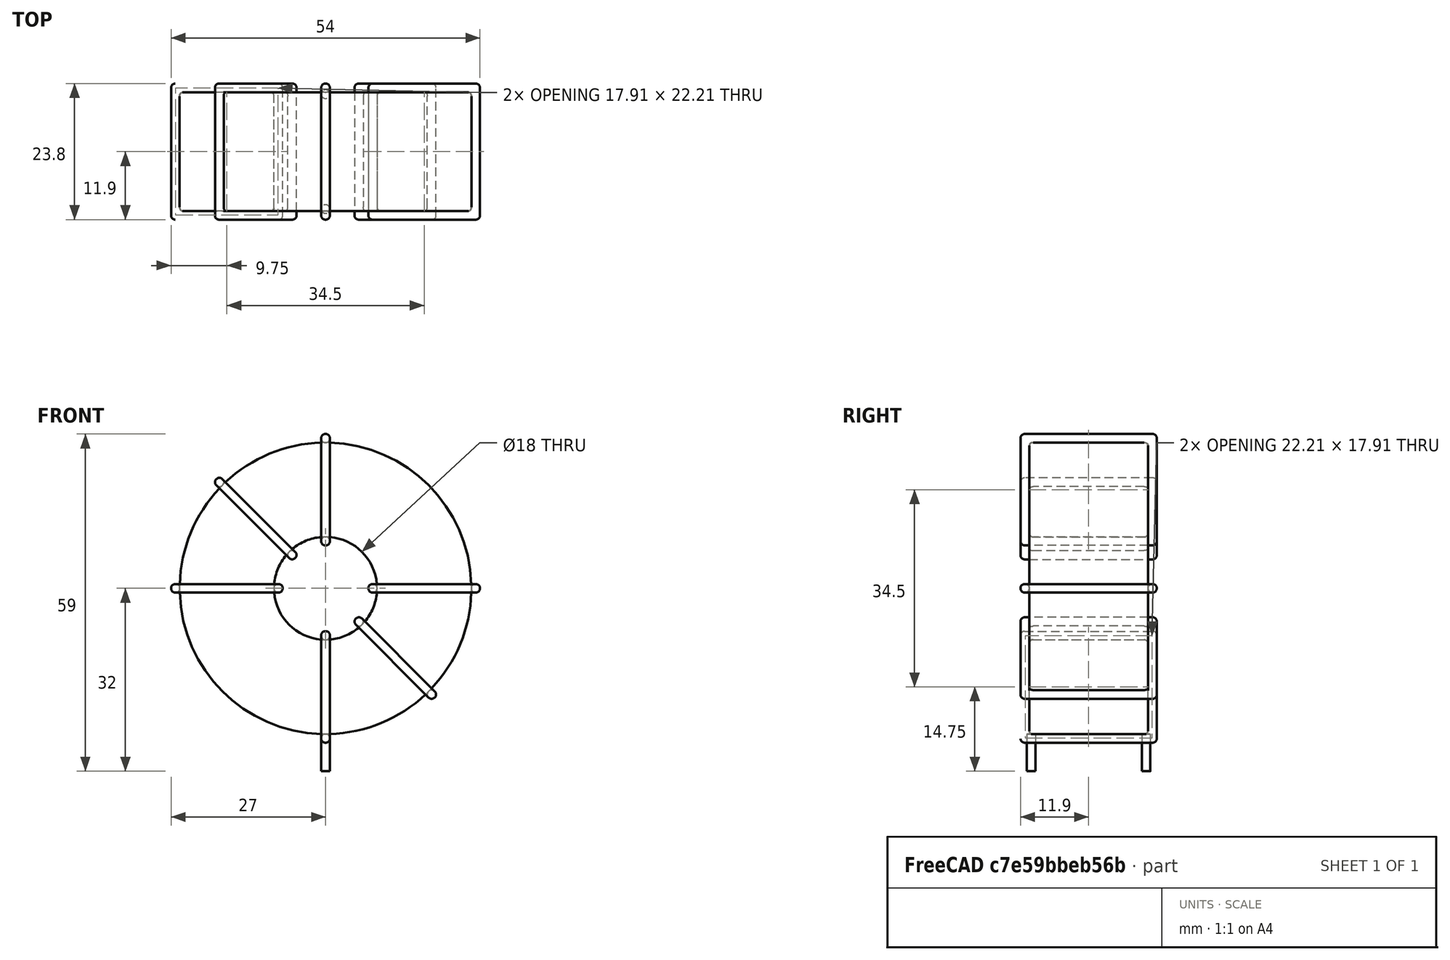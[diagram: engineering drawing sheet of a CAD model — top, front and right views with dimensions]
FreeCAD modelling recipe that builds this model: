
FCSTD DOCUMENT  (FreeCAD 0.16R6703 (Git))
Label: L_Toroid_Vertical_L54.0mm_W23.8mm_P20.10mm_Bourns_5700series
License: All rights reserved
LicenseURL: http://en.wikipedia.org/wiki/All_rights_reserved
objects: Sketcher::SketchObject×6, PartDesign::Pad×6, PartDesign::Fillet×5, Spreadsheet::Sheet×1
note: 23 computed .brp shape members not serialized (recipe doc carries the construction recipe); baked Part::Feature solids carry a one-line shape summary decoded from their .brp

FEATURE [Spreadsheet::Sheet] Spreadsheet  label="dimensions"
  cells = A1=Wx; B1(Wx)=54; C1(WW)=18; D1=54; A2=Wy; B2(Wy)=23.8; D2=23.8; A3=RM; B3(RMx)=20.1; C3(RMy)=0; A4=d_wire; B4(d_wire)=1.5; A5=H; B5(H)=54; A6=offsetx; B6(offsetx)=27
FEATURE [Sketcher::SketchObject] Sketch
  Placement = pos=(0,-10.05,0) rot=(1,0,0;1.5708rad)
  expr: Placement.Base.y = -Spreadsheet.RMx / 2
  expr: Constraints[0] = Spreadsheet.Wx / 2 - Spreadsheet.d_wire
  expr: Constraints[4] = Spreadsheet.WW / 2
  expr: Constraints[2] = Spreadsheet.Wx / 2 + Spreadsheet.d_wire + 0.5
  sketch-geometry (2):
    g0: Circle CenterX=0 CenterY=29 CenterZ=0 NormalX=0 NormalY=0 NormalZ=1 Radius=25.5
    g1: Circle CenterX=0 CenterY=29 CenterZ=0 NormalX=0 NormalY=0 NormalZ=1 Radius=9
  constraints (5):
    c: Radius(g0) = 25.5
    c: DistanceX(g-1,g0) = 0
    c: DistanceY(g-1,g0) = 29
    c: Coincident(g1,g0)
    c: Radius(g1) = 9
FEATURE [PartDesign::Pad] Pad
  Length = 20.8
  Length2 = 100
  Midplane = true
  Placement = pos=(0,-10.05,0) rot=(1,0,0;1.5708rad)
  Sketch = -> Sketch
  Type = 0
  expr: Length = Spreadsheet.Wy - 2 * Spreadsheet.d_wire
FEATURE [Sketcher::SketchObject] Sketch001
  Placement = pos=(0,0,2) rot=(0,0,1;0rad)
  expr: Placement.Base.z = 0.5 + Spreadsheet.d_wire
  expr: Constraints[4] = Spreadsheet.RMy
  expr: Constraints[2] = -Spreadsheet.RMx
  expr: Constraints[1] = Spreadsheet.d_wire / 2
  sketch-geometry (2):
    g0: Circle CenterX=0 CenterY=0 CenterZ=0 NormalX=0 NormalY=0 NormalZ=1 Radius=0.75
    g1: Circle CenterX=0 CenterY=-20.1 CenterZ=0 NormalX=0 NormalY=0 NormalZ=1 Radius=0.75
  constraints (5):
    c: Equal(g0,g1)
    c: Radius(g0) = 0.75
    c: DistanceY(g-1,g1) = -20.1
    c: Coincident(g0,g-1)
    c: DistanceX(g-1,g1) = 0
FEATURE [PartDesign::Pad] Pad001
  Length = 1.5
  Length2 = 5
  Placement = pos=(0,0,2) rot=(0,0,1;0rad)
  Reversed = true
  Sketch = -> Sketch001
  Type = 4
  expr: Length2 = 3.5 + Spreadsheet.d_wire
  expr: Length = Spreadsheet.d_wire
FEATURE [PartDesign::Fillet] Fillet
  Base = -> Pad [Edge6,Edge3,Edge2]
  Placement = pos=(0,-10.05,0) rot=(1,0,0;1.5708rad)
  Radius = 0.5
FEATURE [Sketcher::SketchObject] Sketch003
  Placement = pos=(0,1.85,29) rot=(1,0,0;3.14159rad)
  expr: Constraints[18] = Spreadsheet.d_wire
  expr: Constraints[16] = Spreadsheet.d_wire
  expr: Constraints[19] = Spreadsheet.d_wire
  expr: Constraints[17] = Spreadsheet.d_wire
  expr: Placement.Base.y = -1 * (Spreadsheet.RMx - Spreadsheet.Wy) / 2
  expr: Constraints[21] = (Spreadsheet.Wx - Spreadsheet.WW) / 2 - Spreadsheet.d_wire
  expr: Constraints[22] = Spreadsheet.Wx / 2 - Spreadsheet.d_wire
  expr: Constraints[43] = Spreadsheet.d_wire
  expr: Constraints[48] = Spreadsheet.Wx - Spreadsheet.d_wire * 2
  expr: Constraints[49] = Spreadsheet.Wy
  expr: Placement.Base.z = Spreadsheet.Wx / 2 + Spreadsheet.d_wire + 0.5
  sketch-geometry (16):
    g0: LineSegment StartX=-7.5 StartY=0 StartZ=0 EndX=-27 EndY=0 EndZ=0
    g1: LineSegment StartX=-27 StartY=0 StartZ=0 EndX=-27 EndY=23.8 EndZ=0
    g2: LineSegment StartX=-27 StartY=23.8 StartZ=0 EndX=-7.5 EndY=23.8 EndZ=0
    g3: LineSegment StartX=-7.5 StartY=23.8 StartZ=0 EndX=-7.5 EndY=0 EndZ=0
    g4: LineSegment StartX=-25.5 StartY=22.3 StartZ=0 EndX=-9 EndY=22.3 EndZ=0
    g5: LineSegment StartX=-9 StartY=22.3 StartZ=0 EndX=-9 EndY=1.5 EndZ=0
    g6: LineSegment StartX=-9 StartY=1.5 StartZ=0 EndX=-25.5 EndY=1.5 EndZ=0
    g7: LineSegment StartX=-25.5 StartY=1.5 StartZ=0 EndX=-25.5 EndY=22.3 EndZ=0
    g8: LineSegment StartX=7.5 StartY=23.8 StartZ=0 EndX=27 EndY=23.8 EndZ=0
    g9: LineSegment StartX=27 StartY=23.8 StartZ=0 EndX=27 EndY=0 EndZ=0
    g10: LineSegment StartX=27 StartY=0 StartZ=0 EndX=7.5 EndY=0 EndZ=0
    g11: LineSegment StartX=7.5 StartY=0 StartZ=0 EndX=7.5 EndY=23.8 EndZ=0
    g12: LineSegment StartX=9 StartY=22.3 StartZ=0 EndX=25.5 EndY=22.3 EndZ=0
    g13: LineSegment StartX=25.5 StartY=22.3 StartZ=0 EndX=25.5 EndY=1.5 EndZ=0
    g14: LineSegment StartX=25.5 StartY=1.5 StartZ=0 EndX=9 EndY=1.5 EndZ=0
    g15: LineSegment StartX=9 StartY=1.5 StartZ=0 EndX=9 EndY=22.3 EndZ=0
  constraints (50):
    c: Horizontal(g0)
    c: Coincident(g1,g0)
    c: Vertical(g1)
    c: Coincident(g2,g1)
    c: Horizontal(g2)
    c: Coincident(g3,g2)
    c: Coincident(g3,g0)
    c: Vertical(g3)
    c: Coincident(g4,g5)
    c: Coincident(g5,g6)
    c: Coincident(g6,g7)
    c: Coincident(g7,g4)
    c: Horizontal(g4)
    c: Horizontal(g6)
    c: Vertical(g5)
    c: Vertical(g7)
    c: DistanceX(g1,g4) = 1.5
    c: DistanceY(g4,g1) = 1.5
    c: DistanceX(g5,g0) = 1.5
    c: DistanceY(g0,g5) = 1.5
    c: DistanceY(g-1,g0) = 0
    c: DistanceX(g6,g6) = 16.5
    c: DistanceX(g6,g-1) = 25.5
    c: Coincident(g8,g9)
    c: Coincident(g9,g10)
    c: Coincident(g10,g11)
    c: Coincident(g11,g8)
    c: Horizontal(g8)
    c: Horizontal(g10)
    c: Vertical(g9)
    c: Vertical(g11)
    c: Coincident(g12,g13)
    c: Coincident(g13,g14)
    c: Coincident(g14,g15)
    c: Coincident(g15,g12)
    c: Horizontal(g12)
    c: Horizontal(g14)
    c: Vertical(g13)
    c: Vertical(g15)
    c: DistanceY(g8,g2) = 0
    c: DistanceY(g10,g0) = 0
    c: DistanceY(g14,g5) = 0
    c: DistanceY(g12,g4) = 0
    c: DistanceX(g8,g12) = 1.5
    c: Equal(g8,g2)
    c: Equal(g12,g4)
    c: Equal(g9,g1)
    c: Equal(g13,g7)
    c: DistanceX(g4,g12) = 51
    c: DistanceY(g0,g1) = 23.8
FEATURE [PartDesign::Pad] Pad002
  Length = 1.5
  Length2 = 100
  Midplane = true
  Placement = pos=(0,1.85,29) rot=(1,0,0;3.14159rad)
  Sketch = -> Sketch003
  Type = 0
  expr: Length = Spreadsheet.d_wire
FEATURE [PartDesign::Fillet] Fillet001
  Base = -> Pad002 [Edge38,Edge41,Edge42,Edge43,Edge29,Edge32,Edge33,Edge34,Edge25,Edge35,Edge36,Edge13,Edge14,Edge15,Edge16,Edge17,Edge18,Edge19,Edge1,Edge2,Edge3,Edge4,Edge5,Edge6,Edge7,Edge37,Edge39,Edge40,Edge20,Edge23,Edge24,Edge21,Edge22,Edge8,Edge9,Edge10,Edge11,Edge12,Edge26,Edge27,+8 more]
  Placement = pos=(0,1.85,29) rot=(1,0,0;3.14159rad)
  Radius = 0.705
  expr: Radius = Spreadsheet.d_wire * 0.47
FEATURE [Sketcher::SketchObject] Sketch004
  Placement = pos=(0,1.85,29) rot=(0.92388,0,0.382683;3.14159rad)
  expr: Constraints[18] = Spreadsheet.d_wire
  expr: Constraints[16] = Spreadsheet.d_wire
  expr: Constraints[19] = Spreadsheet.d_wire
  expr: Constraints[17] = Spreadsheet.d_wire
  expr: Placement.Base.y = -1 * (Spreadsheet.RMx - Spreadsheet.Wy) / 2
  expr: Constraints[21] = (Spreadsheet.Wx - Spreadsheet.WW) / 2 - Spreadsheet.d_wire
  expr: Constraints[22] = Spreadsheet.Wx / 2 - Spreadsheet.d_wire
  expr: Constraints[43] = Spreadsheet.d_wire
  expr: Constraints[48] = Spreadsheet.Wx - 2 * Spreadsheet.d_wire
  expr: Constraints[49] = Spreadsheet.Wy
  expr: Placement.Base.z = Spreadsheet.Wx / 2 + Spreadsheet.d_wire + 0.5
  sketch-geometry (16):
    g0: LineSegment StartX=-7.5 StartY=0 StartZ=0 EndX=-27 EndY=0 EndZ=0
    g1: LineSegment StartX=-27 StartY=0 StartZ=0 EndX=-27 EndY=23.8 EndZ=0
    g2: LineSegment StartX=-27 StartY=23.8 StartZ=0 EndX=-7.5 EndY=23.8 EndZ=0
    g3: LineSegment StartX=-7.5 StartY=23.8 StartZ=0 EndX=-7.5 EndY=0 EndZ=0
    g4: LineSegment StartX=-25.5 StartY=22.3 StartZ=0 EndX=-9 EndY=22.3 EndZ=0
    g5: LineSegment StartX=-9 StartY=22.3 StartZ=0 EndX=-9 EndY=1.5 EndZ=0
    g6: LineSegment StartX=-9 StartY=1.5 StartZ=0 EndX=-25.5 EndY=1.5 EndZ=0
    g7: LineSegment StartX=-25.5 StartY=1.5 StartZ=0 EndX=-25.5 EndY=22.3 EndZ=0
    g8: LineSegment StartX=7.5 StartY=23.8 StartZ=0 EndX=27 EndY=23.8 EndZ=0
    g9: LineSegment StartX=27 StartY=23.8 StartZ=0 EndX=27 EndY=0 EndZ=0
    g10: LineSegment StartX=27 StartY=0 StartZ=0 EndX=7.5 EndY=0 EndZ=0
    g11: LineSegment StartX=7.5 StartY=0 StartZ=0 EndX=7.5 EndY=23.8 EndZ=0
    g12: LineSegment StartX=9 StartY=22.3 StartZ=0 EndX=25.5 EndY=22.3 EndZ=0
    g13: LineSegment StartX=25.5 StartY=22.3 StartZ=0 EndX=25.5 EndY=1.5 EndZ=0
    g14: LineSegment StartX=25.5 StartY=1.5 StartZ=0 EndX=9 EndY=1.5 EndZ=0
    g15: LineSegment StartX=9 StartY=1.5 StartZ=0 EndX=9 EndY=22.3 EndZ=0
  constraints (50):
    c: Horizontal(g0)
    c: Coincident(g1,g0)
    c: Vertical(g1)
    c: Coincident(g2,g1)
    c: Horizontal(g2)
    c: Coincident(g3,g2)
    c: Coincident(g3,g0)
    c: Vertical(g3)
    c: Coincident(g4,g5)
    c: Coincident(g5,g6)
    c: Coincident(g6,g7)
    c: Coincident(g7,g4)
    c: Horizontal(g4)
    c: Horizontal(g6)
    c: Vertical(g5)
    c: Vertical(g7)
    c: DistanceX(g1,g4) = 1.5
    c: DistanceY(g4,g1) = 1.5
    c: DistanceX(g5,g0) = 1.5
    c: DistanceY(g0,g5) = 1.5
    c: DistanceY(g-1,g0) = 0
    c: DistanceX(g6,g6) = 16.5
    c: DistanceX(g6,g-1) = 25.5
    c: Coincident(g8,g9)
    c: Coincident(g9,g10)
    c: Coincident(g10,g11)
    c: Coincident(g11,g8)
    c: Horizontal(g8)
    c: Horizontal(g10)
    c: Vertical(g9)
    c: Vertical(g11)
    c: Coincident(g12,g13)
    c: Coincident(g13,g14)
    c: Coincident(g14,g15)
    c: Coincident(g15,g12)
    c: Horizontal(g12)
    c: Horizontal(g14)
    c: Vertical(g13)
    c: Vertical(g15)
    c: DistanceY(g8,g2) = 0
    c: DistanceY(g10,g0) = 0
    c: DistanceY(g14,g5) = 0
    c: DistanceY(g12,g4) = 0
    c: DistanceX(g8,g12) = 1.5
    c: Equal(g8,g2)
    c: Equal(g12,g4)
    c: Equal(g9,g1)
    c: Equal(g13,g7)
    c: DistanceX(g4,g12) = 51
    c: DistanceY(g0,g1) = 23.8
FEATURE [PartDesign::Pad] Pad003
  Length = 1.5
  Length2 = 100
  Midplane = true
  Placement = pos=(0,1.85,29) rot=(0.92388,0,0.382683;3.14159rad)
  Sketch = -> Sketch004
  Type = 0
  expr: Length = Spreadsheet.d_wire
FEATURE [PartDesign::Fillet] Fillet002
  Base = -> Pad003 [Edge38,Edge41,Edge42,Edge43,Edge29,Edge32,Edge33,Edge34,Edge25,Edge35,Edge36,Edge13,Edge14,Edge15,Edge16,Edge17,Edge18,Edge19,Edge1,Edge2,Edge3,Edge4,Edge5,Edge6,Edge7,Edge37,Edge39,Edge40,Edge20,Edge23,Edge24,Edge21,Edge22,Edge8,Edge9,Edge10,Edge11,Edge12,Edge26,Edge27,+8 more]
  Placement = pos=(0,1.85,29) rot=(0.92388,0,0.382683;3.14159rad)
  Radius = 0.705
  expr: Radius = Spreadsheet.d_wire * 0.47
FEATURE [Sketcher::SketchObject] Sketch005
  Placement = pos=(0,1.85,29) rot=(0.92388,0,-0.382683;3.14159rad)
  expr: Constraints[18] = Spreadsheet.d_wire
  expr: Constraints[16] = Spreadsheet.d_wire
  expr: Constraints[19] = Spreadsheet.d_wire
  expr: Constraints[17] = Spreadsheet.d_wire
  expr: Placement.Base.y = -1 * (Spreadsheet.RMx - Spreadsheet.Wy) / 2
  expr: Constraints[21] = (Spreadsheet.Wx - Spreadsheet.WW) / 2 - Spreadsheet.d_wire
  expr: Constraints[22] = Spreadsheet.Wx / 2 - Spreadsheet.d_wire
  expr: Constraints[43] = Spreadsheet.d_wire
  expr: Constraints[48] = Spreadsheet.Wx - 2 * Spreadsheet.d_wire
  expr: Constraints[49] = Spreadsheet.Wy
  expr: Placement.Base.z = Spreadsheet.Wx / 2 + Spreadsheet.d_wire + 0.5
  sketch-geometry (16):
    g0: LineSegment StartX=-7.5 StartY=0 StartZ=0 EndX=-27 EndY=0 EndZ=0
    g1: LineSegment StartX=-27 StartY=0 StartZ=0 EndX=-27 EndY=23.8 EndZ=0
    g2: LineSegment StartX=-27 StartY=23.8 StartZ=0 EndX=-7.5 EndY=23.8 EndZ=0
    g3: LineSegment StartX=-7.5 StartY=23.8 StartZ=0 EndX=-7.5 EndY=0 EndZ=0
    g4: LineSegment StartX=-25.5 StartY=22.3 StartZ=0 EndX=-9 EndY=22.3 EndZ=0
    g5: LineSegment StartX=-9 StartY=22.3 StartZ=0 EndX=-9 EndY=1.5 EndZ=0
    g6: LineSegment StartX=-9 StartY=1.5 StartZ=0 EndX=-25.5 EndY=1.5 EndZ=0
    g7: LineSegment StartX=-25.5 StartY=1.5 StartZ=0 EndX=-25.5 EndY=22.3 EndZ=0
    g8: LineSegment StartX=7.5 StartY=23.8 StartZ=0 EndX=27 EndY=23.8 EndZ=0
    g9: LineSegment StartX=27 StartY=23.8 StartZ=0 EndX=27 EndY=0 EndZ=0
    g10: LineSegment StartX=27 StartY=0 StartZ=0 EndX=7.5 EndY=0 EndZ=0
    g11: LineSegment StartX=7.5 StartY=0 StartZ=0 EndX=7.5 EndY=23.8 EndZ=0
    g12: LineSegment StartX=9 StartY=22.3 StartZ=0 EndX=25.5 EndY=22.3 EndZ=0
    g13: LineSegment StartX=25.5 StartY=22.3 StartZ=0 EndX=25.5 EndY=1.5 EndZ=0
    g14: LineSegment StartX=25.5 StartY=1.5 StartZ=0 EndX=9 EndY=1.5 EndZ=0
    g15: LineSegment StartX=9 StartY=1.5 StartZ=0 EndX=9 EndY=22.3 EndZ=0
  constraints (50):
    c: Horizontal(g0)
    c: Coincident(g1,g0)
    c: Vertical(g1)
    c: Coincident(g2,g1)
    c: Horizontal(g2)
    c: Coincident(g3,g2)
    c: Coincident(g3,g0)
    c: Vertical(g3)
    c: Coincident(g4,g5)
    c: Coincident(g5,g6)
    c: Coincident(g6,g7)
    c: Coincident(g7,g4)
    c: Horizontal(g4)
    c: Horizontal(g6)
    c: Vertical(g5)
    c: Vertical(g7)
    c: DistanceX(g1,g4) = 1.5
    c: DistanceY(g4,g1) = 1.5
    c: DistanceX(g5,g0) = 1.5
    c: DistanceY(g0,g5) = 1.5
    c: DistanceY(g-1,g0) = 0
    c: DistanceX(g6,g6) = 16.5
    c: DistanceX(g6,g-1) = 25.5
    c: Coincident(g8,g9)
    c: Coincident(g9,g10)
    c: Coincident(g10,g11)
    c: Coincident(g11,g8)
    c: Horizontal(g8)
    c: Horizontal(g10)
    c: Vertical(g9)
    c: Vertical(g11)
    c: Coincident(g12,g13)
    c: Coincident(g13,g14)
    c: Coincident(g14,g15)
    c: Coincident(g15,g12)
    c: Horizontal(g12)
    c: Horizontal(g14)
    c: Vertical(g13)
    c: Vertical(g15)
    c: DistanceY(g8,g2) = 0
    c: DistanceY(g10,g0) = 0
    c: DistanceY(g14,g5) = 0
    c: DistanceY(g12,g4) = 0
    c: DistanceX(g8,g12) = 1.5
    c: Equal(g8,g2)
    c: Equal(g12,g4)
    c: Equal(g9,g1)
    c: Equal(g13,g7)
    c: DistanceX(g4,g12) = 51
    c: DistanceY(g0,g1) = 23.8
FEATURE [PartDesign::Pad] Pad004
  Length = 1.5
  Length2 = 100
  Midplane = true
  Placement = pos=(0,1.85,29) rot=(0.92388,0,-0.382683;3.14159rad)
  Sketch = -> Sketch005
  Type = 0
  expr: Length = Spreadsheet.d_wire
FEATURE [PartDesign::Fillet] Fillet003
  Base = -> Pad004 [Edge38,Edge41,Edge42,Edge43,Edge29,Edge32,Edge33,Edge34,Edge25,Edge35,Edge36,Edge13,Edge14,Edge15,Edge16,Edge17,Edge18,Edge19,Edge1,Edge2,Edge3,Edge4,Edge5,Edge6,Edge7,Edge37,Edge39,Edge40,Edge20,Edge23,Edge24,Edge21,Edge22,Edge8,Edge9,Edge10,Edge11,Edge12,Edge26,Edge27,+8 more]
  Placement = pos=(0,1.85,29) rot=(0.92388,0,-0.382683;3.14159rad)
  Radius = 0.705
  expr: Radius = Spreadsheet.d_wire * 0.47
FEATURE [Sketcher::SketchObject] Sketch006
  Placement = pos=(0,1.85,29) rot=(0.707107,0,0.707107;3.14159rad)
  expr: Constraints[18] = Spreadsheet.d_wire
  expr: Constraints[16] = Spreadsheet.d_wire
  expr: Constraints[19] = Spreadsheet.d_wire
  expr: Constraints[17] = Spreadsheet.d_wire
  expr: Placement.Base.y = -1 * (Spreadsheet.RMx - Spreadsheet.Wy) / 2
  expr: Constraints[21] = (Spreadsheet.Wx - Spreadsheet.WW) / 2 - Spreadsheet.d_wire
  expr: Constraints[22] = Spreadsheet.Wx / 2 - Spreadsheet.d_wire
  expr: Constraints[43] = Spreadsheet.d_wire
  expr: Constraints[48] = Spreadsheet.Wx - Spreadsheet.d_wire * 2
  expr: Constraints[49] = Spreadsheet.Wy
  expr: Placement.Base.z = Spreadsheet.Wx / 2 + Spreadsheet.d_wire + 0.5
  sketch-geometry (16):
    g0: LineSegment StartX=-7.5 StartY=0 StartZ=0 EndX=-27 EndY=0 EndZ=0
    g1: LineSegment StartX=-27 StartY=0 StartZ=0 EndX=-27 EndY=23.8 EndZ=0
    g2: LineSegment StartX=-27 StartY=23.8 StartZ=0 EndX=-7.5 EndY=23.8 EndZ=0
    g3: LineSegment StartX=-7.5 StartY=23.8 StartZ=0 EndX=-7.5 EndY=0 EndZ=0
    g4: LineSegment StartX=-25.5 StartY=22.3 StartZ=0 EndX=-9 EndY=22.3 EndZ=0
    g5: LineSegment StartX=-9 StartY=22.3 StartZ=0 EndX=-9 EndY=1.5 EndZ=0
    g6: LineSegment StartX=-9 StartY=1.5 StartZ=0 EndX=-25.5 EndY=1.5 EndZ=0
    g7: LineSegment StartX=-25.5 StartY=1.5 StartZ=0 EndX=-25.5 EndY=22.3 EndZ=0
    g8: LineSegment StartX=7.5 StartY=23.8 StartZ=0 EndX=27 EndY=23.8 EndZ=0
    g9: LineSegment StartX=27 StartY=23.8 StartZ=0 EndX=27 EndY=0 EndZ=0
    g10: LineSegment StartX=27 StartY=0 StartZ=0 EndX=7.5 EndY=0 EndZ=0
    g11: LineSegment StartX=7.5 StartY=0 StartZ=0 EndX=7.5 EndY=23.8 EndZ=0
    g12: LineSegment StartX=9 StartY=22.3 StartZ=0 EndX=25.5 EndY=22.3 EndZ=0
    g13: LineSegment StartX=25.5 StartY=22.3 StartZ=0 EndX=25.5 EndY=1.5 EndZ=0
    g14: LineSegment StartX=25.5 StartY=1.5 StartZ=0 EndX=9 EndY=1.5 EndZ=0
    g15: LineSegment StartX=9 StartY=1.5 StartZ=0 EndX=9 EndY=22.3 EndZ=0
  constraints (50):
    c: Horizontal(g0)
    c: Coincident(g1,g0)
    c: Vertical(g1)
    c: Coincident(g2,g1)
    c: Horizontal(g2)
    c: Coincident(g3,g2)
    c: Coincident(g3,g0)
    c: Vertical(g3)
    c: Coincident(g4,g5)
    c: Coincident(g5,g6)
    c: Coincident(g6,g7)
    c: Coincident(g7,g4)
    c: Horizontal(g4)
    c: Horizontal(g6)
    c: Vertical(g5)
    c: Vertical(g7)
    c: DistanceX(g1,g4) = 1.5
    c: DistanceY(g4,g1) = 1.5
    c: DistanceX(g5,g0) = 1.5
    c: DistanceY(g0,g5) = 1.5
    c: DistanceY(g-1,g0) = 0
    c: DistanceX(g6,g6) = 16.5
    c: DistanceX(g6,g-1) = 25.5
    c: Coincident(g8,g9)
    c: Coincident(g9,g10)
    c: Coincident(g10,g11)
    c: Coincident(g11,g8)
    c: Horizontal(g8)
    c: Horizontal(g10)
    c: Vertical(g9)
    c: Vertical(g11)
    c: Coincident(g12,g13)
    c: Coincident(g13,g14)
    c: Coincident(g14,g15)
    c: Coincident(g15,g12)
    c: Horizontal(g12)
    c: Horizontal(g14)
    c: Vertical(g13)
    c: Vertical(g15)
    c: DistanceY(g8,g2) = 0
    c: DistanceY(g10,g0) = 0
    c: DistanceY(g14,g5) = 0
    c: DistanceY(g12,g4) = 0
    c: DistanceX(g8,g12) = 1.5
    c: Equal(g8,g2)
    c: Equal(g12,g4)
    c: Equal(g9,g1)
    c: Equal(g13,g7)
    c: DistanceX(g4,g12) = 51
    c: DistanceY(g0,g1) = 23.8
FEATURE [PartDesign::Pad] Pad005
  Length = 1.5
  Length2 = 100
  Midplane = true
  Placement = pos=(0,1.85,29) rot=(0.707107,0,0.707107;3.14159rad)
  Sketch = -> Sketch006
  Type = 0
  expr: Length = Spreadsheet.d_wire
FEATURE [PartDesign::Fillet] Fillet004
  Base = -> Pad005 [Edge38,Edge41,Edge42,Edge43,Edge29,Edge32,Edge33,Edge34,Edge25,Edge35,Edge36,Edge13,Edge14,Edge15,Edge16,Edge17,Edge18,Edge19,Edge1,Edge2,Edge3,Edge4,Edge5,Edge6,Edge7,Edge37,Edge39,Edge40,Edge20,Edge23,Edge24,Edge21,Edge22,Edge8,Edge9,Edge10,Edge11,Edge12,Edge26,Edge27,+8 more]
  Placement = pos=(0,1.85,29) rot=(0.707107,0,0.707107;3.14159rad)
  Radius = 0.705
  expr: Radius = Spreadsheet.d_wire * 0.47
